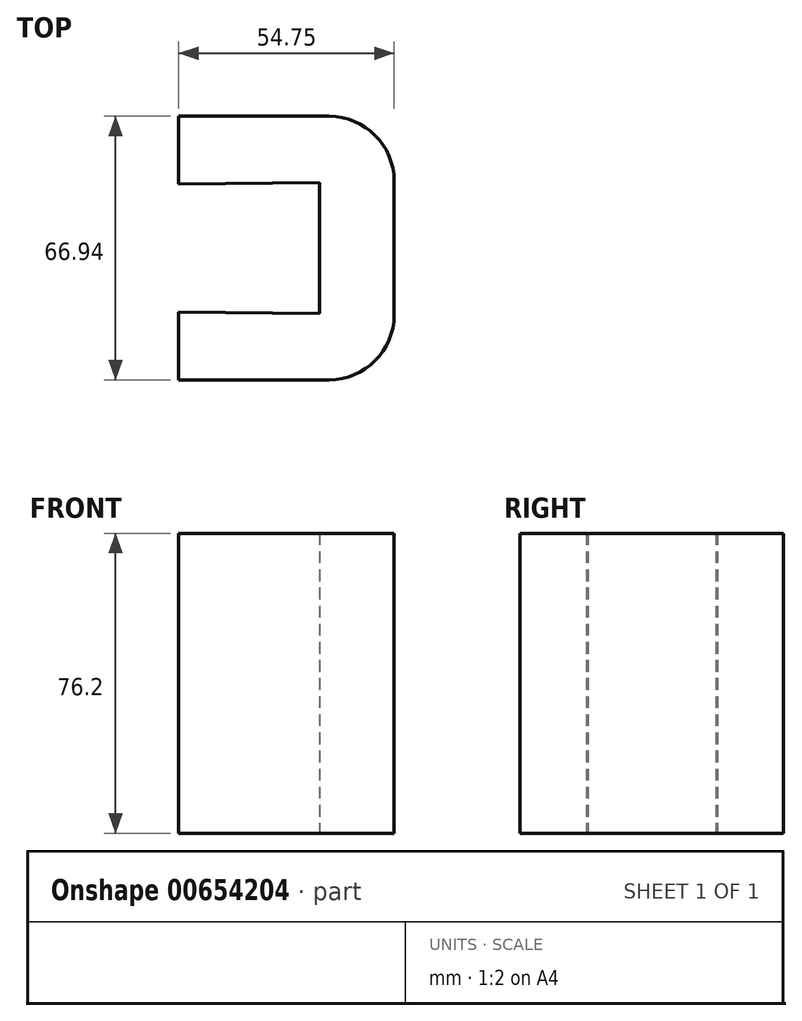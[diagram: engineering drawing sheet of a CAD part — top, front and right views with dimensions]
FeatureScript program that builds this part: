
annotation { "Feature Type Name" : "Feature", "Feature Type Description" : "" }
export const myFeature = defineFeature(function(context is Context, id is Id, definition is map)
    precondition{}
    {
        {
            var Q0;
            Q0=qCreatedBy(makeId("Top.planeOp"),FACE);
            var sketch = newSketch(context, id + "F0", { "sketchPlane" : qUnion([Q0])});
            skLineSegment(sketch, "E0", {"start": v(10.81, -16.25) * mm, "end": v(10.81, -33.47) * mm});
            skLineSegment(sketch, "E1", {"start": v(10.81, -33.47) * mm, "end": v(49.05, -33.47) * mm});
            skLineSegment(sketch, "E2", {"start": v(65.56, -16.96) * mm, "end": v(65.56, 0) * mm});
            skLineSegment(sketch, "E3", {"start": v(65.56, 0) * mm, "end": v(46.55, 0) * mm});
            skLineSegment(sketch, "E4", {"start": v(46.55, 0) * mm, "end": v(46.55, -16.63) * mm});
            skLineSegment(sketch, "E5", {"start": v(46.55, -16.63) * mm, "end": v(10.81, -16.25) * mm});
            skLineSegment(sketch, "E6.MirrorCS", {"start": v(46.55, 16.63) * mm, "end": v(10.81, 16.25) * mm});
            skLineSegment(sketch, "E7.MirrorCS", {"start": v(46.55, 0) * mm, "end": v(46.55, 16.63) * mm});
            skLineSegment(sketch, "E8.MirrorCS", {"start": v(10.81, 16.25) * mm, "end": v(10.81, 33.47) * mm});
            skLineSegment(sketch, "E9.MirrorCS", {"start": v(65.56, 16.96) * mm, "end": v(65.56, 0) * mm});
            skLineSegment(sketch, "E10.MirrorCS", {"start": v(10.81, 33.47) * mm, "end": v(49.05, 33.47) * mm});
            skPoint(sketch, "E11.visualSharp", {"position": v(65.56, 33.47) * mm});
            skArc(sketch, "E11.filletArc", {"start": v(65.56, 16.96) * mm, "mid": v(60.73, 28.63) * mm, "end": v(49.05, 33.47) * mm});
            skPoint(sketch, "E12.visualSharp", {"position": v(65.56, -33.47) * mm});
            skArc(sketch, "E12.filletArc", {"start": v(49.05, -33.47) * mm, "mid": v(60.73, -28.63) * mm, "end": v(65.56, -16.96) * mm});
            skSolve(sketch);
        }
        {
            var Q0;
            Q0=makeQuery(id+"F0.imprint","IMPRINT",FACE,{"disambiguationData":[TD([[makeQuery(id+"F0.imprint","IMPRINT",EDGE,{"derivedFrom":sQuery(id+"F0.wireOp",EDGE,"E3")}),-1.0]])]});
            var Q1;
            Q1=makeQuery(id+"F0.imprint","IMPRINT",FACE,{"disambiguationData":[TD([[makeQuery(id+"F0.imprint","IMPRINT",EDGE,{"derivedFrom":sQuery(id+"F0.wireOp",EDGE,"E0")}),1.0]])]});
            extrude(context, id + "F1", {"entities" : qUnion([Q0, Q1]), "depth" : 76.2 * mm, "offsetDistance" : 25.4 * mm});
        }
    });
